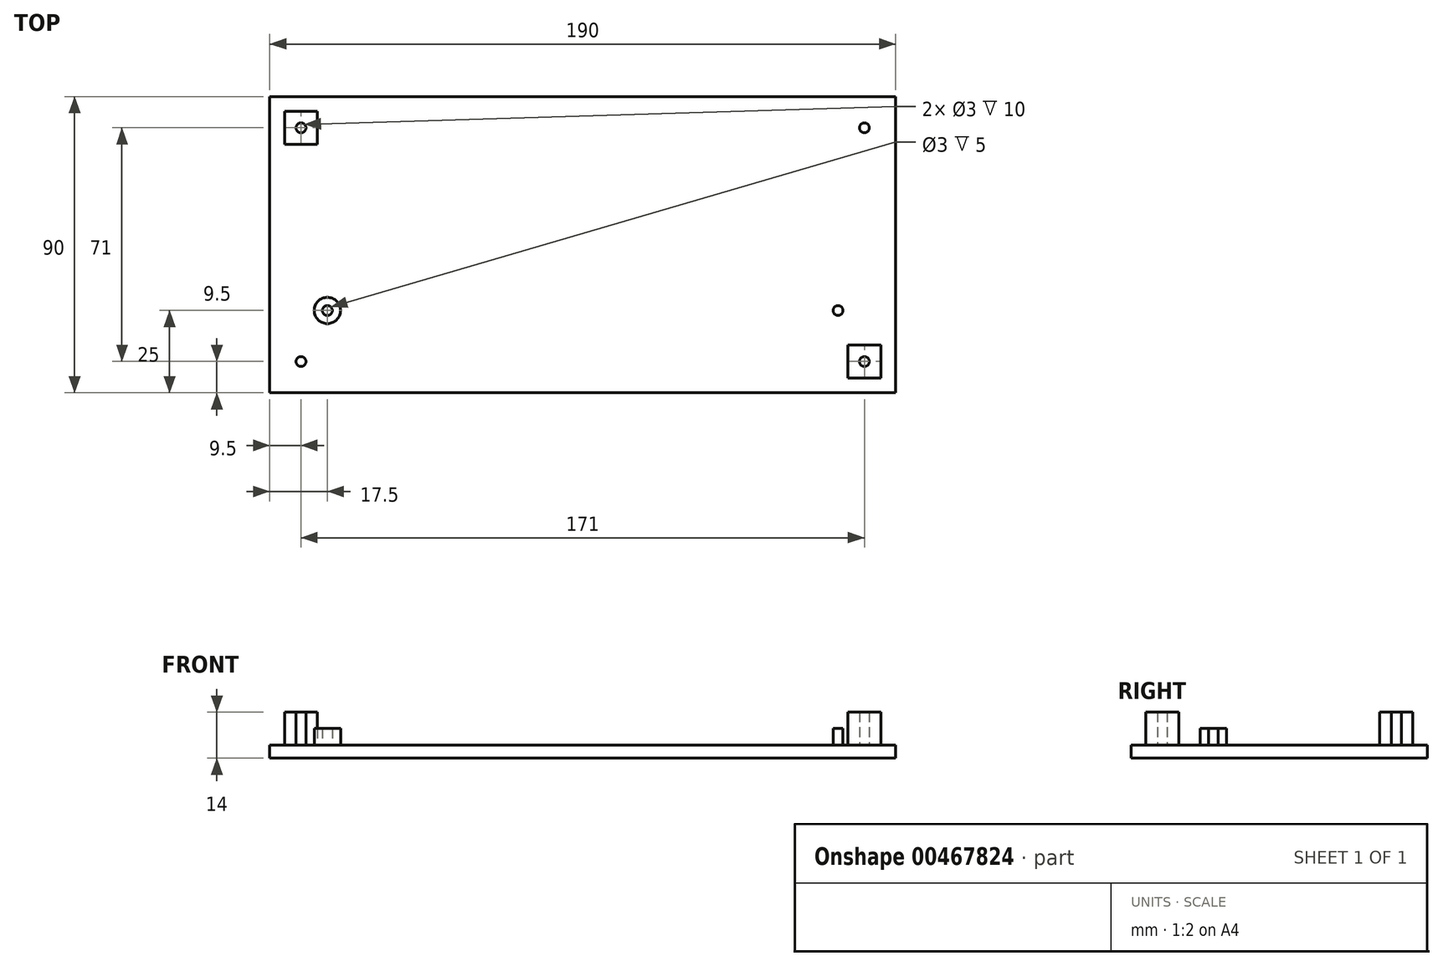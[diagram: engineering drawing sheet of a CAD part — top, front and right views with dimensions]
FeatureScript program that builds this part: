
annotation { "Feature Type Name" : "Feature", "Feature Type Description" : "" }
export const myFeature = defineFeature(function(context is Context, id is Id, definition is map)
    precondition{}
    {
        {
            var Q0;
            Q0=qCreatedBy(makeId("Top.planeOp"),FACE);
            var sketch = newSketch(context, id + "F0", { "sketchPlane" : qUnion([Q0])});
            skLineSegment(sketch, "E0.bottom", {"start": v(-95, 45) * mm, "end": v(95, 45) * mm});
            skLineSegment(sketch, "E0.top", {"start": v(-95, -45) * mm, "end": v(95, -45) * mm});
            skLineSegment(sketch, "E0.left", {"start": v(-95, 45) * mm, "end": v(-95, -45) * mm});
            skLineSegment(sketch, "E0.right", {"start": v(95, 45) * mm, "end": v(95, -45) * mm});
            skLineSegment(sketch, "E1.bottom", {"start": v(-90.5, 40.5) * mm, "end": v(-80.5, 40.5) * mm});
            skLineSegment(sketch, "E1.top", {"start": v(-90.5, 30.5) * mm, "end": v(-80.5, 30.5) * mm});
            skLineSegment(sketch, "E1.left", {"start": v(-90.5, 40.5) * mm, "end": v(-90.5, 30.5) * mm});
            skLineSegment(sketch, "E1.right", {"start": v(-80.5, 40.5) * mm, "end": v(-80.5, 30.5) * mm});
            skPoint(sketch, "E2.centerSnap0", {"position": v(-90.5, 35.5) * mm});
            skLineSegment(sketch, "E3", {"start": v(-85.5, 40.5) * mm, "end": v(-85.5, 30.5) * mm, "construction": true});
            skLineSegment(sketch, "E4", {"start": v(-90.5, 35.5) * mm, "end": v(-80.5, 35.5) * mm, "construction": true});
            skCircle(sketch, "E5", {"center": v(-85.5, 35.5) * mm, "radius": 1.5 * mm});
            skCircle(sketch, "E6.MirrorC", {"center": v(85.5, 35.5) * mm, "radius": 1.5 * mm});
            skLineSegment(sketch, "E7.MirrorCS", {"start": v(90.5, 40.5) * mm, "end": v(90.5, 30.5) * mm});
            skLineSegment(sketch, "E8.MirrorCS", {"start": v(90.5, 40.5) * mm, "end": v(80.5, 40.5) * mm});
            skLineSegment(sketch, "E9.MirrorCS", {"start": v(90.5, 30.5) * mm, "end": v(80.5, 30.5) * mm});
            skLineSegment(sketch, "E10.MirrorCS", {"start": v(80.5, 40.5) * mm, "end": v(80.5, 30.5) * mm});
            skCircle(sketch, "E11.MirrorC", {"center": v(-85.5, -35.5) * mm, "radius": 1.5 * mm});
            skLineSegment(sketch, "E12.MirrorCS", {"start": v(-90.5, -40.5) * mm, "end": v(-90.5, -30.5) * mm});
            skLineSegment(sketch, "E13.MirrorCS", {"start": v(-90.5, -40.5) * mm, "end": v(-80.5, -40.5) * mm});
            skLineSegment(sketch, "E14.MirrorCS", {"start": v(-90.5, -30.5) * mm, "end": v(-80.5, -30.5) * mm});
            skLineSegment(sketch, "E15.MirrorCS", {"start": v(-80.5, -40.5) * mm, "end": v(-80.5, -30.5) * mm});
            skCircle(sketch, "E16.MirrorC", {"center": v(85.5, -35.5) * mm, "radius": 1.5 * mm});
            skLineSegment(sketch, "E17.MirrorCS", {"start": v(90.5, -40.5) * mm, "end": v(80.5, -40.5) * mm});
            skLineSegment(sketch, "E18.MirrorCS", {"start": v(80.5, -40.5) * mm, "end": v(80.5, -30.5) * mm});
            skLineSegment(sketch, "E19.MirrorCS", {"start": v(90.5, -40.5) * mm, "end": v(90.5, -30.5) * mm});
            skLineSegment(sketch, "E20.MirrorCS", {"start": v(90.5, -30.5) * mm, "end": v(80.5, -30.5) * mm});
            skLineSegment(sketch, "E21", {"start": v(-77.5, -20) * mm, "end": v(-77.5, -45) * mm, "construction": true});
            skLineSegment(sketch, "E22", {"start": v(77.5, -20) * mm, "end": v(77.5, -45) * mm, "construction": true});
            skLineSegment(sketch, "E23", {"start": v(77.5, -20) * mm, "end": v(-77.5, -20) * mm, "construction": true});
            skCircle(sketch, "E24", {"center": v(-77.5, -20) * mm, "radius": 4 * mm});
            skCircle(sketch, "E25", {"center": v(-77.5, -20) * mm, "radius": 1.5 * mm});
            skCircle(sketch, "E26.MirrorC", {"center": v(77.5, -20) * mm, "radius": 1.5 * mm});
            skCircle(sketch, "E27.MirrorC", {"center": v(77.5, -20) * mm, "radius": 4 * mm});
            skSolve(sketch);
        }
        {
            var Q0;
            Q0=makeQuery(id+"F0.imprint","IMPRINT",FACE,{"disambiguationData":[TD([[makeQuery(id+"F0.imprint","IMPRINT",EDGE,{"derivedFrom":sQuery(id+"F0.wireOp",EDGE,"E0.bottom")}),-1.0]])]});
            var Q1;
            Q1=makeQuery(id+"F0.imprint","IMPRINT",FACE,{"disambiguationData":[TD([[makeQuery(id+"F0.imprint","IMPRINT",EDGE,{"derivedFrom":sQuery(id+"F0.wireOp",EDGE,"E1.bottom")}),-1.0]])]});
            var Q2;
            Q2=makeQuery(id+"F0.imprint","IMPRINT",FACE,{"disambiguationData":[TD([[makeQuery(id+"F0.imprint","IMPRINT",EDGE,{"derivedFrom":sQuery(id+"F0.wireOp",EDGE,"E26.MirrorC")}),1.0]])]});
            var Q3;
            Q3=makeQuery(id+"F0.imprint","IMPRINT",FACE,{"disambiguationData":[TD([[makeQuery(id+"F0.imprint","IMPRINT",EDGE,{"derivedFrom":sQuery(id+"F0.wireOp",EDGE,"E24")}),1.0]])]});
            var Q4;
            Q4=makeQuery(id+"F0.imprint","IMPRINT",FACE,{"disambiguationData":[TD([[makeQuery(id+"F0.imprint","IMPRINT",EDGE,{"derivedFrom":sQuery(id+"F0.wireOp",EDGE,"E16.MirrorC")}),-1.0]])]});
            var Q5;
            Q5=makeQuery(id+"F0.imprint","IMPRINT",FACE,{"disambiguationData":[TD([[makeQuery(id+"F0.imprint","IMPRINT",EDGE,{"derivedFrom":sQuery(id+"F0.wireOp",EDGE,"E11.MirrorC")}),1.0]])]});
            var Q6;
            Q6=makeQuery(id+"F0.imprint","IMPRINT",FACE,{"disambiguationData":[TD([[makeQuery(id+"F0.imprint","IMPRINT",EDGE,{"derivedFrom":sQuery(id+"F0.wireOp",EDGE,"E6.MirrorC")}),1.0]])]});
            var Q7;
            Q7=makeQuery(id+"F0.imprint","IMPRINT",FACE,{"disambiguationData":[TD([[makeQuery(id+"F0.imprint","IMPRINT",EDGE,{"derivedFrom":sQuery(id+"F0.wireOp",EDGE,"E16.MirrorC")}),1.0]])]});
            var Q8;
            Q8=makeQuery(id+"F0.imprint","IMPRINT",FACE,{"disambiguationData":[TD([[makeQuery(id+"F0.imprint","IMPRINT",EDGE,{"derivedFrom":sQuery(id+"F0.wireOp",EDGE,"E11.MirrorC")}),-1.0]])]});
            var Q9;
            Q9=makeQuery(id+"F0.imprint","IMPRINT",FACE,{"disambiguationData":[TD([[makeQuery(id+"F0.imprint","IMPRINT",EDGE,{"derivedFrom":sQuery(id+"F0.wireOp",EDGE,"E6.MirrorC")}),-1.0]])]});
            var Q10;
            Q10=makeQuery(id+"F0.imprint","IMPRINT",FACE,{"disambiguationData":[TD([[makeQuery(id+"F0.imprint","IMPRINT",EDGE,{"derivedFrom":sQuery(id+"F0.wireOp",EDGE,"E5")}),1.0]])]});
            var Q11;
            Q11=makeQuery(id+"F0.imprint","IMPRINT",FACE,{"disambiguationData":[TD([[makeQuery(id+"F0.imprint","IMPRINT",EDGE,{"derivedFrom":sQuery(id+"F0.wireOp",EDGE,"E26.MirrorC")}),-1.0]])]});
            var Q12;
            Q12=makeQuery(id+"F0.imprint","IMPRINT",FACE,{"disambiguationData":[TD([[makeQuery(id+"F0.imprint","IMPRINT",EDGE,{"derivedFrom":sQuery(id+"F0.wireOp",EDGE,"E25")}),1.0]])]});
            extrude(context, id + "F1", {"entities" : qUnion([Q0, Q1, Q2, Q3, Q4, Q5, Q6, Q7, Q8, Q9, Q10, Q11, Q12]), "depth" : -4 * mm});
        }
        {
            var Q0;
            Q0=makeQuery(id+"F0.imprint","IMPRINT",FACE,{"disambiguationData":[TD([[makeQuery(id+"F0.imprint","IMPRINT",EDGE,{"derivedFrom":sQuery(id+"F0.wireOp",EDGE,"E26.MirrorC")}),1.0]])]});
            var Q1;
            Q1=makeQuery(id+"F0.imprint","IMPRINT",FACE,{"disambiguationData":[TD([[makeQuery(id+"F0.imprint","IMPRINT",EDGE,{"derivedFrom":sQuery(id+"F0.wireOp",EDGE,"E24")}),1.0]])]});
            extrude(context, id + "F2", {"entities" : qUnion([Q0, Q1]), "operationType" : NewBodyOperationType.ADD, "depth" : 5 * mm});
        }
        {
            var Q0;
            Q0=makeQuery(id+"F0.imprint","IMPRINT",FACE,{"disambiguationData":[TD([[makeQuery(id+"F0.imprint","IMPRINT",EDGE,{"derivedFrom":sQuery(id+"F0.wireOp",EDGE,"E11.MirrorC")}),1.0]])]});
            var Q1;
            Q1=makeQuery(id+"F0.imprint","IMPRINT",FACE,{"disambiguationData":[TD([[makeQuery(id+"F0.imprint","IMPRINT",EDGE,{"derivedFrom":sQuery(id+"F0.wireOp",EDGE,"E1.bottom")}),-1.0]])]});
            var Q2;
            Q2=makeQuery(id+"F0.imprint","IMPRINT",FACE,{"disambiguationData":[TD([[makeQuery(id+"F0.imprint","IMPRINT",EDGE,{"derivedFrom":sQuery(id+"F0.wireOp",EDGE,"E6.MirrorC")}),1.0]])]});
            var Q3;
            Q3=makeQuery(id+"F0.imprint","IMPRINT",FACE,{"disambiguationData":[TD([[makeQuery(id+"F0.imprint","IMPRINT",EDGE,{"derivedFrom":sQuery(id+"F0.wireOp",EDGE,"E16.MirrorC")}),-1.0]])]});
            extrude(context, id + "F3", {"entities" : qUnion([Q0, Q1, Q2, Q3]), "operationType" : NewBodyOperationType.ADD, "depth" : 10 * mm});
        }
    });
